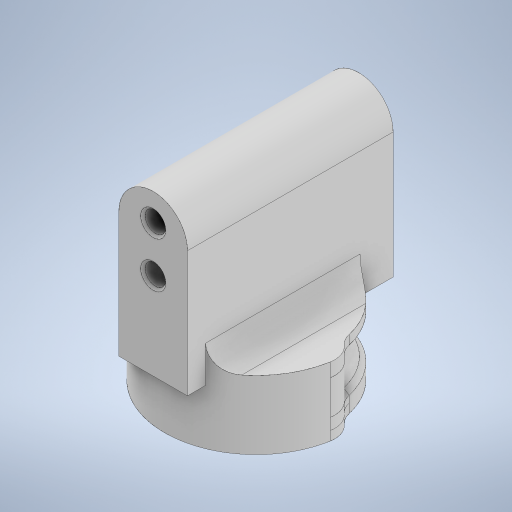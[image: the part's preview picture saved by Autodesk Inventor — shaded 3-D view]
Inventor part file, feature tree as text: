
AUTODESK INVENTOR PART (.ipt)
format: ipt  version: 2023 (Build 270158000, 158)  size: 458,752 bytes
history: native  units: mm
features: extrude x10, sketch x8, fillet x3, chamfer x2, other x1, projected_geometry x1
ambient origin geometry x8: Origin, YZ Plane, XZ Plane, XY Plane, X Axis, Y Axis, Z Axis, Center Point
bodies: Body1 (feature_tree)
feature tree (25):
  other  "솔리드1"
  extrude  "돌출1"  Depth=15.0mm
  extrude  "돌출2"  Depth=35.0mm
  fillet  "모깎기1"  Radius=45.0mm
  chamfer  "모따기1"  Distance=4.5mm
  sketch  "스케치3"
  extrude  "돌출3"  Depth=4.5mm
  extrude  "돌출5"  Depth=10.0mm
  extrude  "돌출6"  Depth=30.0mm TaperAngle=0.0deg
  fillet  "모깎기4"  Radius=7.5mm
  extrude  "돌출7"  Depth=0.5mm TaperAngle=45.0deg
  extrude  "돌출8"  Depth=40.0mm
  chamfer  "모따기2"  Distance=2.0mm
  fillet  "모깎기5"  Radius=3.0mm
  extrude  "돌출11"  Depth=10.0mm TaperAngle=0.0deg
  extrude  "돌출12"  Depth=7.5mm TaperAngle=0.0deg
  extrude  "돌출13"  Depth=3.0mm TaperAngle=0.0deg
  sketch  "스케치1"
  sketch  "스케치2"
  sketch  "스케치5"
  sketch  "스케치6"
  sketch  "스케치8"
  sketch  "스케치9"
  projected_geometry  "투영된 루프2"
  sketch  "스케치10"
